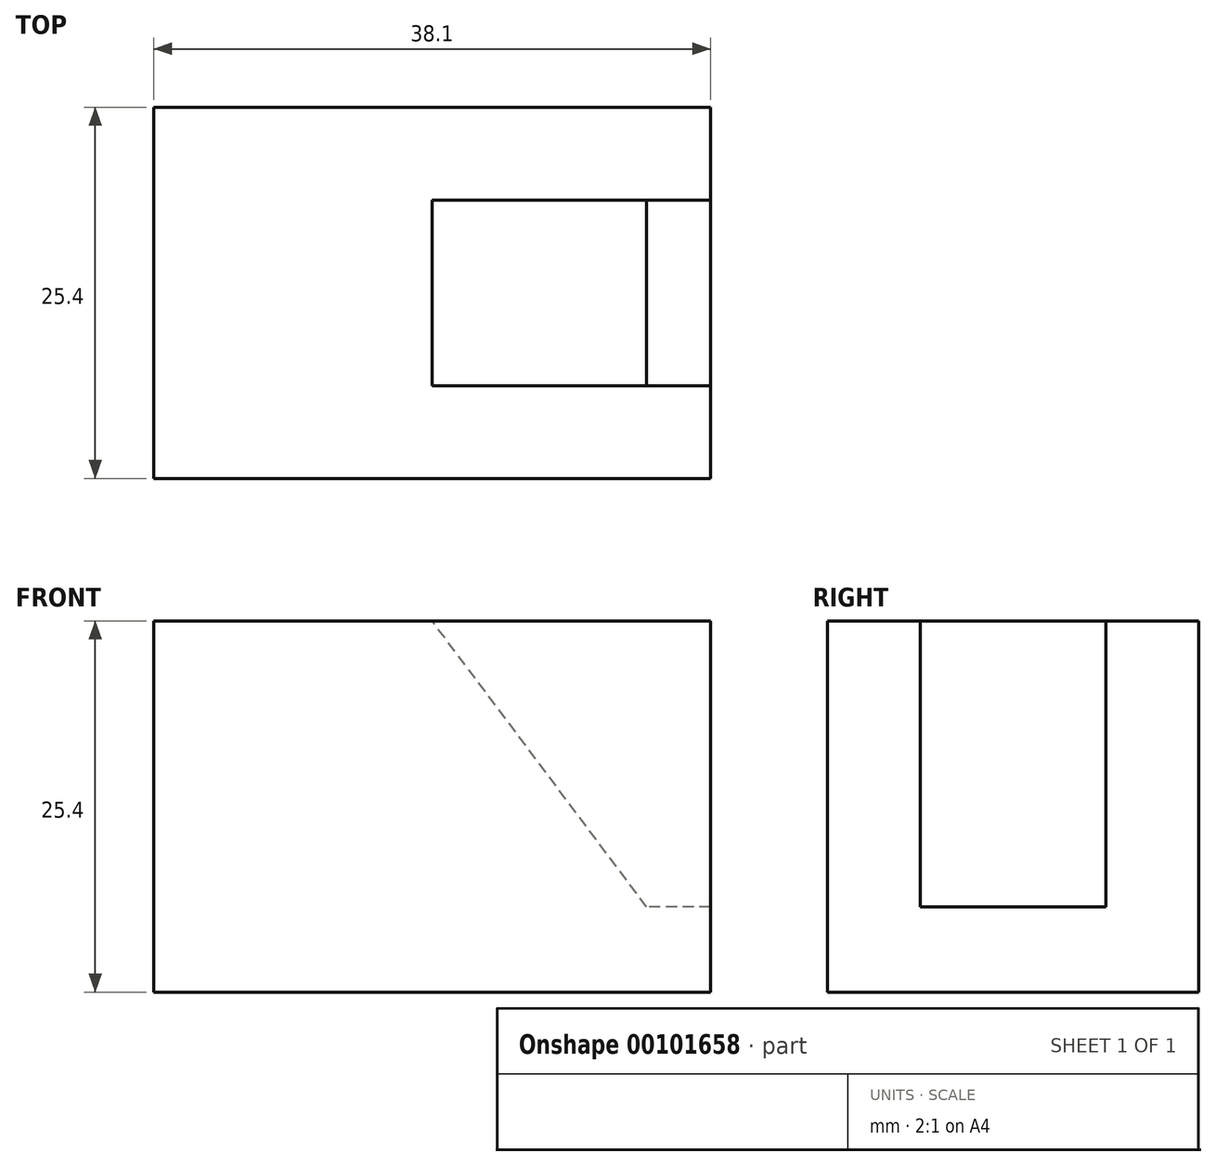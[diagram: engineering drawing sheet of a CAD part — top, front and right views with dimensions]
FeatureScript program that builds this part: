
annotation { "Feature Type Name" : "Feature", "Feature Type Description" : "" }
export const myFeature = defineFeature(function(context is Context, id is Id, definition is map)
    precondition{}
    {
        {
            var Q0;
            Q0=qCreatedBy(makeId("Front.planeOp"),FACE);
            var sketch = newSketch(context, id + "F0", { "sketchPlane" : qUnion([Q0])});
            skLineSegment(sketch, "E0", {"start": v(0, 0) * mm, "end": v(0, 25.4) * mm});
            skLineSegment(sketch, "E1", {"start": v(0, 25.4) * mm, "end": v(19.05, 25.4) * mm});
            skLineSegment(sketch, "E2", {"start": v(19.05, 25.4) * mm, "end": v(19.05, 0) * mm});
            skLineSegment(sketch, "E3", {"start": v(19.05, 0) * mm, "end": v(0, 0) * mm});
            skLineSegment(sketch, "E4", {"start": v(0, 0) * mm, "end": v(38.1, 0) * mm});
            skLineSegment(sketch, "E5", {"start": v(38.1, 0) * mm, "end": v(19.05, 25.4) * mm});
            skSolve(sketch);
        }
        {
            var Q0;
            {var subQ0=sQuery(id+"F0.wireOp",EDGE,"E0");Q0=makeQuery(id+"F0.imprint","IMPRINT",FACE,{"disambiguationData":[TD([[makeQuery(id+"F0.imprint","IMPRINT",EDGE,{"derivedFrom":subQ0}),-1.0]])]});}
            extrude(context, id + "F1", {"entities" : qUnion([Q0]), "oppositeDirection" : true, "depth" : 25.4 * mm});
        }
        {
            var Q0;
            Q0=qCreatedBy(makeId("Right.planeOp"),FACE);
            var sketch = newSketch(context, id + "F2", { "sketchPlane" : qUnion([Q0])});
            skLineSegment(sketch, "E6", {"start": v(0, 0) * mm, "end": v(0, 25.4) * mm});
            skLineSegment(sketch, "E7", {"start": v(0, 25.4) * mm, "end": v(6.35, 25.4) * mm});
            skLineSegment(sketch, "E8", {"start": v(6.35, 25.4) * mm, "end": v(6.35, 5.83) * mm});
            skLineSegment(sketch, "E9", {"start": v(6.35, 5.83) * mm, "end": v(19.05, 5.83) * mm});
            skLineSegment(sketch, "E10", {"start": v(19.05, 5.83) * mm, "end": v(19.05, 25.4) * mm});
            skLineSegment(sketch, "E11", {"start": v(19.05, 25.4) * mm, "end": v(25.4, 25.4) * mm});
            skLineSegment(sketch, "E12", {"start": v(25.4, 25.4) * mm, "end": v(25.4, 0) * mm});
            skLineSegment(sketch, "E13", {"start": v(25.4, 0) * mm, "end": v(0, 0) * mm});
            skSolve(sketch);
        }
        {
            var Q0;
            Q0=makeQuery(id+"F2.imprint","IMPRINT",FACE,{"disambiguationData":[TD([[makeQuery(id+"F2.imprint","IMPRINT",EDGE,{"derivedFrom":sQuery(id+"F2.wireOp",EDGE,"E6")}),-1.0]])]});
            extrude(context, id + "F3", {"entities" : qUnion([Q0]), "operationType" : NewBodyOperationType.ADD, "depth" : 38.1 * mm});
        }
        {
            var Q0;
            {var subQ0=sQuery(id+"F0.wireOp",EDGE,"E5");Q0=makeQuery(id+"F0.imprint","IMPRINT",FACE,{"disambiguationData":[TD([[makeQuery(id+"F0.imprint","IMPRINT",EDGE,{"derivedFrom":subQ0}),1.0]])]});}
            extrude(context, id + "F4", {"entities" : qUnion([Q0]), "operationType" : NewBodyOperationType.ADD, "oppositeDirection" : true, "depth" : 25.4 * mm});
        }
    });
